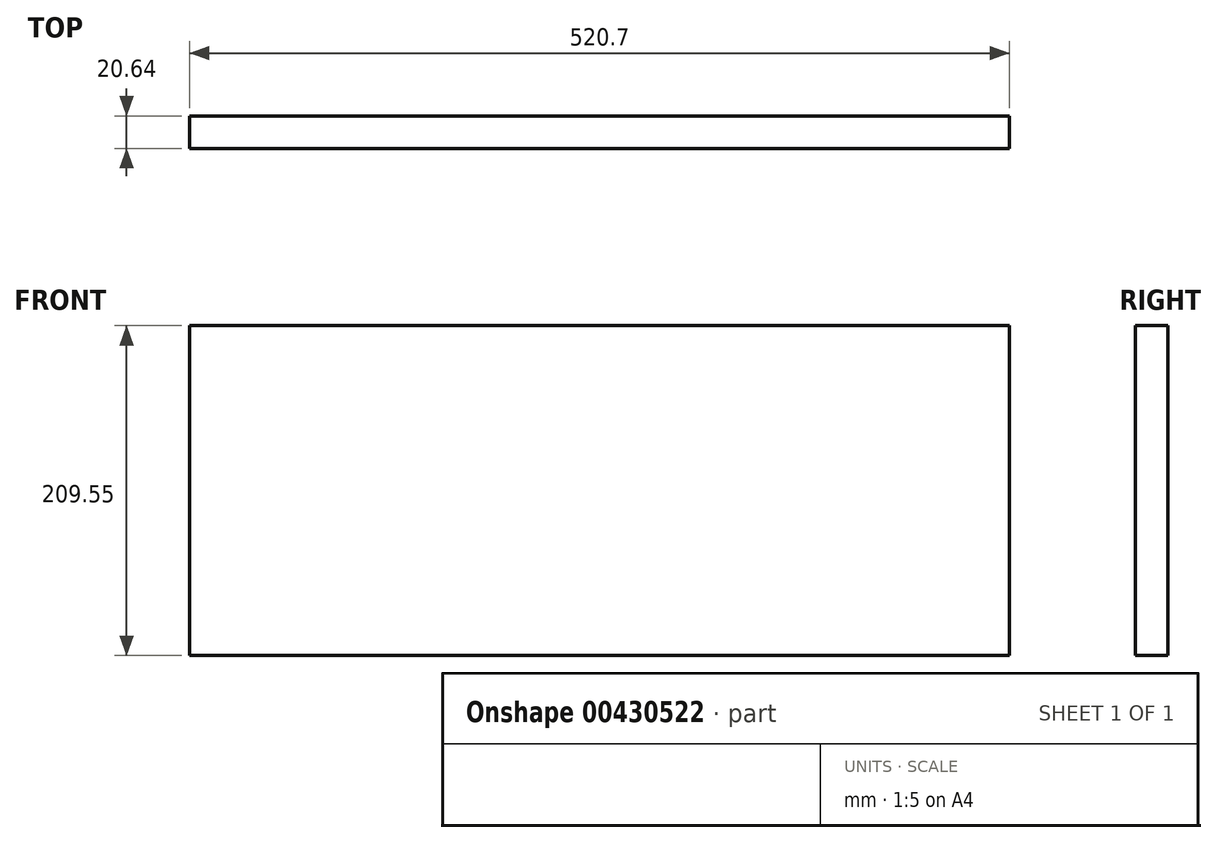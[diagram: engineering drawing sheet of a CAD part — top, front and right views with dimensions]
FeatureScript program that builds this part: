
annotation { "Feature Type Name" : "Feature", "Feature Type Description" : "" }
export const myFeature = defineFeature(function(context is Context, id is Id, definition is map)
    precondition{}
    {
        {
            var Q0;
            Q0=qCreatedBy(makeId("Top.planeOp"),FACE);
            var sketch = newSketch(context, id + "F0", { "sketchPlane" : qUnion([Q0])});
            skLineSegment(sketch, "E0", {"start": v(-260.35, 0) * mm, "end": v(260.35, 0) * mm});
            skLineSegment(sketch, "E1", {"start": v(260.35, 0) * mm, "end": v(260.35, 20.64) * mm});
            skLineSegment(sketch, "E2", {"start": v(260.35, 20.64) * mm, "end": v(-260.35, 20.64) * mm});
            skLineSegment(sketch, "E3", {"start": v(-260.35, 20.64) * mm, "end": v(-260.35, 0) * mm});
            skSolve(sketch);
        }
        {
            var Q0;
            Q0=makeQuery(id+"F0.imprint","IMPRINT",FACE,{"disambiguationData":[TD([[makeQuery(id+"F0.imprint","IMPRINT",EDGE,{"derivedFrom":sQuery(id+"F0.wireOp",EDGE,"E0")}),1.0]])]});
            extrude(context, id + "F1", {"entities" : qUnion([Q0]), "oppositeDirection" : true, "depth" : 209.55 * mm, "offsetDistance" : 25.4 * mm});
        }
    });
